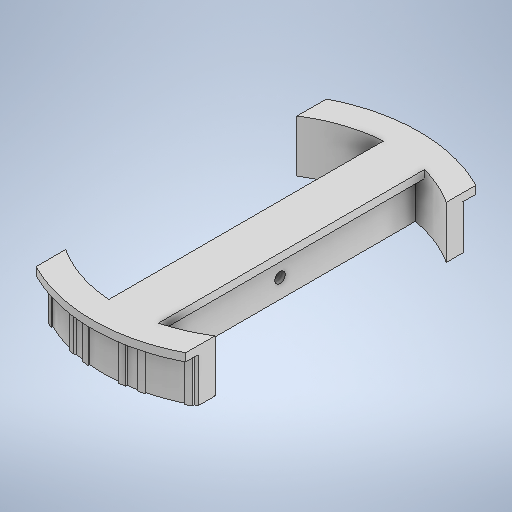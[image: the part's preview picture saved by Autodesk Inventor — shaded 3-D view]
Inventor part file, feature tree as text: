
AUTODESK INVENTOR PART (.ipt)
format: ipt  version: 2025 (Build 290162010, 162A)  size: 510,976 bytes
history: native  units: mm
features: sketch x10, extrude x9, pattern_circular x1, hole x1
ambient origin geometry x8: Origin, YZ Plane, XZ Plane, XY Plane, X Axis, Y Axis, Z Axis, Center Point
bodies: Solid1 (feature_tree)
feature tree (21):
  extrude  "Extrusion1"  Depth=15.0mm
  extrude  "Extrusion2"  Depth=5.0mm
  extrude  "Extrusion3"  TaperAngle=0.0deg  [1 undecoded]
  extrude  "Extrusion5"  Depth=78.1mm
  pattern_circular  "Circular Pattern1"  Count=18 Angle=360.0deg
  extrude  "Extrusion6"  Depth=83.0mm
  extrude  "Extrusion7"  Depth=13.75mm TaperAngle=0.0deg
  extrude  "Extrusion9"  Depth=70.0mm
  extrude  "Extrusion13"  Depth=10.0mm TaperAngle=0.0deg
  extrude  "Extrusion14"  Depth=2.0mm
  hole  "Hole3"  [1 undecoded]
  sketch  "Sketch1"  dims[d0=77.3mm d1=15.0mm]
  sketch  "Sketch2"  dims[d2=25.0mm d3=0.0mm d4=5.0mm]
  sketch  "Sketch3"  dims[d5=55.0mm d6=0.0mm d7=0.0mm]
  sketch  "Sketch9"  dims[d8=165.1mm d9=0.0mm d31=78.1mm]
  sketch  "Sketch11"  dims[d32=1.0mm d33=0.0mm d37=180.0mm d38=360.0deg]
  sketch  "Sketch12"  dims[d40=0.0mm d41=0.0mm d42=83.0mm]
  sketch  "Sketch14"  dims[d43=2.0mm d44=0.0mm d47=13.75mm d48=0.0mm]
  sketch  "Sketch18"  dims[d52=60.0mm d62=70.0mm]
  sketch  "Sketch19"  dims[d63=0.0mm d64=0.0mm d65=10.0mm d66=0.0mm]
  sketch  "Sketch20"  dims[d67=35.0mm d68=6.4mm d69=2.6416mm d70=7.01mm d71=4.0mm d72=2.0mm d73=90.0deg d74=10.979mm d75=0.0mm d56=0.5mm d57=0.872665mm d58=0.5mm d59=0.872665mm d60=0.872665mm d61=0.5mm]
note: 2 required parameter values undecoded (feature->parameter linkage not recoverable at this tier; creation-order binding heuristic only, values carry confidence <= 0.55)
